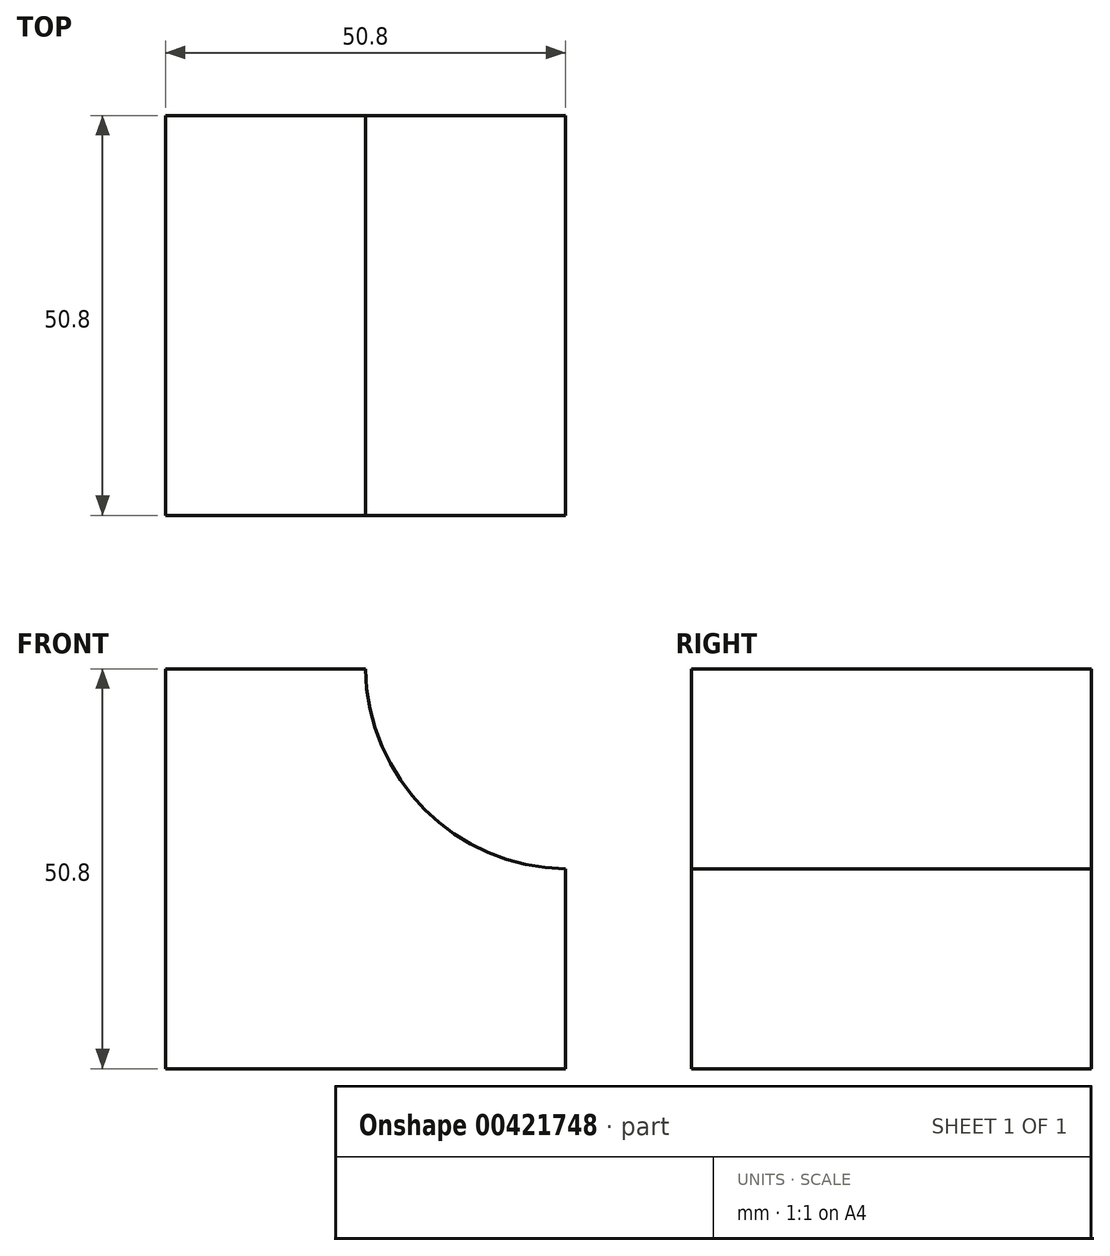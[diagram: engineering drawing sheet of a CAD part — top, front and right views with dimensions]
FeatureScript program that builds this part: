
annotation { "Feature Type Name" : "Feature", "Feature Type Description" : "" }
export const myFeature = defineFeature(function(context is Context, id is Id, definition is map)
    precondition{}
    {
        {
            var Q0;
            Q0=qCreatedBy(makeId("Front.planeOp"),FACE);
            var sketch = newSketch(context, id + "F0", { "sketchPlane" : qUnion([Q0])});
            skLineSegment(sketch, "E0", {"start": v(0, 0) * mm, "end": v(-50.8, 0) * mm});
            skLineSegment(sketch, "E1", {"start": v(-50.8, 0) * mm, "end": v(-50.8, 50.8) * mm});
            skLineSegment(sketch, "E2", {"start": v(-50.8, 50.8) * mm, "end": v(-25.4, 50.8) * mm});
            skLineSegment(sketch, "E3", {"start": v(0, 0) * mm, "end": v(0, 25.4) * mm});
            skArc(sketch, "E4", {"start": v(-25.4, 50.8) * mm, "mid": v(-17.88, 32.92) * mm, "end": v(0, 25.4) * mm});
            skSolve(sketch);
        }
        {
            var Q0;
            Q0=makeQuery(id+"F0.imprint","IMPRINT",FACE,{"disambiguationData":[TD([[makeQuery(id+"F0.imprint","IMPRINT",EDGE,{"derivedFrom":sQuery(id+"F0.wireOp",EDGE,"E0")}),-1.0]])]});
            extrude(context, id + "F1", {"entities" : qUnion([Q0]), "depth" : 50.8 * mm});
        }
    });
